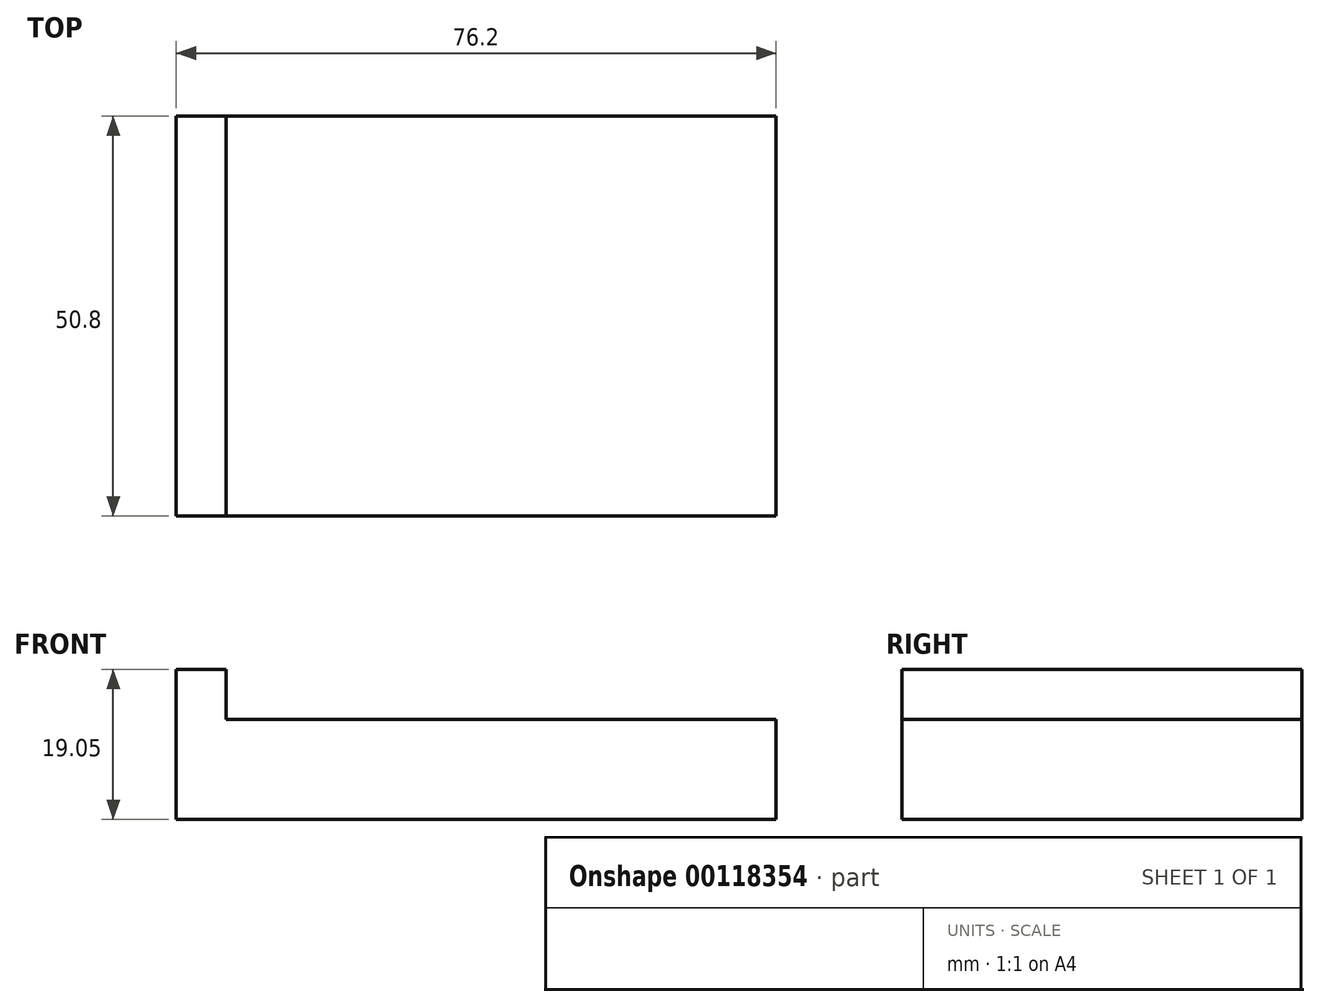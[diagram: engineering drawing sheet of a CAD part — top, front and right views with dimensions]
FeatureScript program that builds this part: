
annotation { "Feature Type Name" : "Feature", "Feature Type Description" : "" }
export const myFeature = defineFeature(function(context is Context, id is Id, definition is map)
    precondition{}
    {
        {
            var Q0;
            Q0=qCreatedBy(makeId("Front.planeOp"),FACE);
            var sketch = newSketch(context, id + "F0", { "sketchPlane" : qUnion([Q0])});
            skLineSegment(sketch, "E0.bottom", {"start": v(-38.1, 6.35) * mm, "end": v(38.1, 6.35) * mm});
            skLineSegment(sketch, "E0.top", {"start": v(-38.1, -6.35) * mm, "end": v(38.1, -6.35) * mm});
            skLineSegment(sketch, "E0.left", {"start": v(-38.1, 6.35) * mm, "end": v(-38.1, -6.35) * mm});
            skLineSegment(sketch, "E0.right", {"start": v(38.1, 6.35) * mm, "end": v(38.1, -6.35) * mm});
            skPoint(sketch, "E0.middle", {"position": v(0, 0) * mm});
            skLineSegment(sketch, "E1.bottom", {"start": v(-38.1, -6.35) * mm, "end": v(-31.75, -6.35) * mm});
            skLineSegment(sketch, "E1.top", {"start": v(-38.1, 12.7) * mm, "end": v(-31.75, 12.7) * mm});
            skLineSegment(sketch, "E1.left", {"start": v(-38.1, -6.35) * mm, "end": v(-38.1, 12.7) * mm});
            skLineSegment(sketch, "E1.right", {"start": v(-31.75, -6.35) * mm, "end": v(-31.75, 12.7) * mm});
            skSolve(sketch);
        }
        {
            var Q0;
            {var subQ5=sQuery(id+"F0.wireOp",EDGE,"E1.bottom");Q0=makeQuery(id+"F0.imprint","IMPRINT",FACE,{"disambiguationData":[TD([[makeQuery(id+"F0.imprint","IMPRINT",EDGE,{"derivedFrom":subQ5}),1.0]])]});}
            var Q1;
            {var subQ5=sQuery(id+"F0.wireOp",EDGE,"E1.top");Q1=makeQuery(id+"F0.imprint","IMPRINT",FACE,{"disambiguationData":[TD([[makeQuery(id+"F0.imprint","IMPRINT",EDGE,{"derivedFrom":subQ5}),-1.0]])]});}
            var Q2;
            {var subQ4=sQuery(id+"F0.wireOp",EDGE,"E0.top");Q2=makeQuery(id+"F0.imprint","IMPRINT",FACE,{"disambiguationData":[TD([[makeQuery(id+"F0.imprint","IMPRINT",EDGE,{"derivedFrom":subQ4}),1.0]])]});}
            extrude(context, id + "F1", {"entities" : qUnion([Q0, Q1, Q2]), "depth" : 25.4 * mm});
        }
        {
            var Q0;
            Q0 = qSketchRegion(id + "F0", true);
            var Q1;
            Q1=makeQuery(id+"F1.opExtrude","CAP_FACE",FACE,{"disambiguationData":[OSD([sQuery(id+"F0.wireOp",EDGE,"E0.bottom"),sQuery(id+"F0.wireOp",EDGE,"E0.top"),sQuery(id+"F0.wireOp",EDGE,"E0.right"),sQuery(id+"F0.wireOp",EDGE,"E1.bottom"),sQuery(id+"F0.wireOp",EDGE,"E1.top"),sQuery(id+"F0.wireOp",EDGE,"E1.left"),sQuery(id+"F0.wireOp",EDGE,"E1.right")])],"isStart":false});
            extrude(context, id + "F2", {"entities" : qUnion([Q0, Q1]), "operationType" : NewBodyOperationType.ADD, "depth" : 25.4 * mm});
        }
    });
